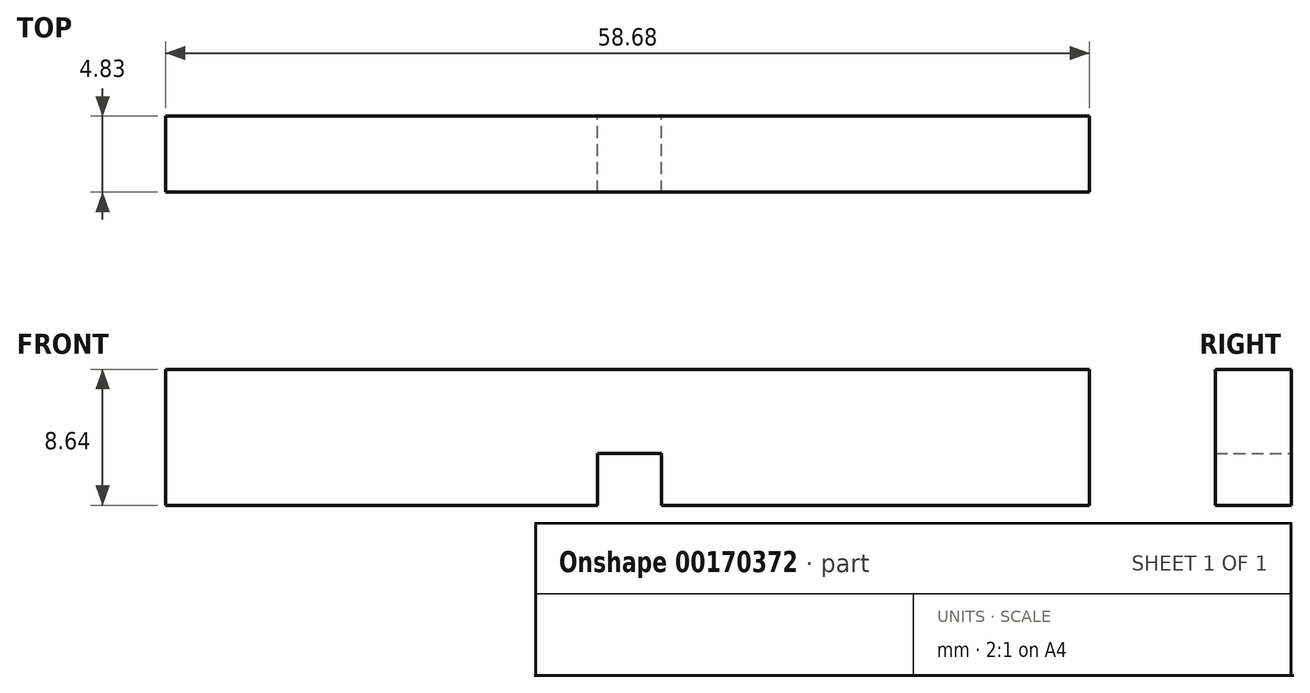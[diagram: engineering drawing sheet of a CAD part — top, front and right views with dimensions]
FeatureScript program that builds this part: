
annotation { "Feature Type Name" : "Feature", "Feature Type Description" : "" }
export const myFeature = defineFeature(function(context is Context, id is Id, definition is map)
    precondition{}
    {
        {
            var Q0;
            Q0=qCreatedBy(makeId("Front.planeOp"),FACE);
            var sketch = newSketch(context, id + "F0", { "sketchPlane" : qUnion([Q0])});
            skLineSegment(sketch, "E0.bottom", {"start": v(29.34, -4.32) * mm, "end": v(2.16, -4.32) * mm});
            skLineSegment(sketch, "E0.top", {"start": v(29.34, 4.32) * mm, "end": v(-29.34, 4.32) * mm});
            skLineSegment(sketch, "E0.left", {"start": v(29.34, -4.32) * mm, "end": v(29.34, 4.32) * mm});
            skLineSegment(sketch, "E0.right", {"start": v(-29.34, -4.32) * mm, "end": v(-29.34, 4.32) * mm});
            skPoint(sketch, "E0.middle", {"position": v(0, 0) * mm});
            skLineSegment(sketch, "E1", {"start": v(2.16, -4.32) * mm, "end": v(2.16, -1.02) * mm});
            skLineSegment(sketch, "E2", {"start": v(2.16, -1.02) * mm, "end": v(-1.9, -1.02) * mm});
            skLineSegment(sketch, "E3", {"start": v(-1.9, -1.02) * mm, "end": v(-1.9, -4.32) * mm});
            skLineSegment(sketch, "E4.trimOffspring", {"start": v(-1.9, -4.32) * mm, "end": v(-29.34, -4.32) * mm});
            skSolve(sketch);
        }
        {
            var Q0;
            Q0 = qSketchRegion(id + "F0", true);
            extrude(context, id + "F1", {"entities" : qUnion([Q0]), "depth" : 4.83 * mm});
        }
    });
